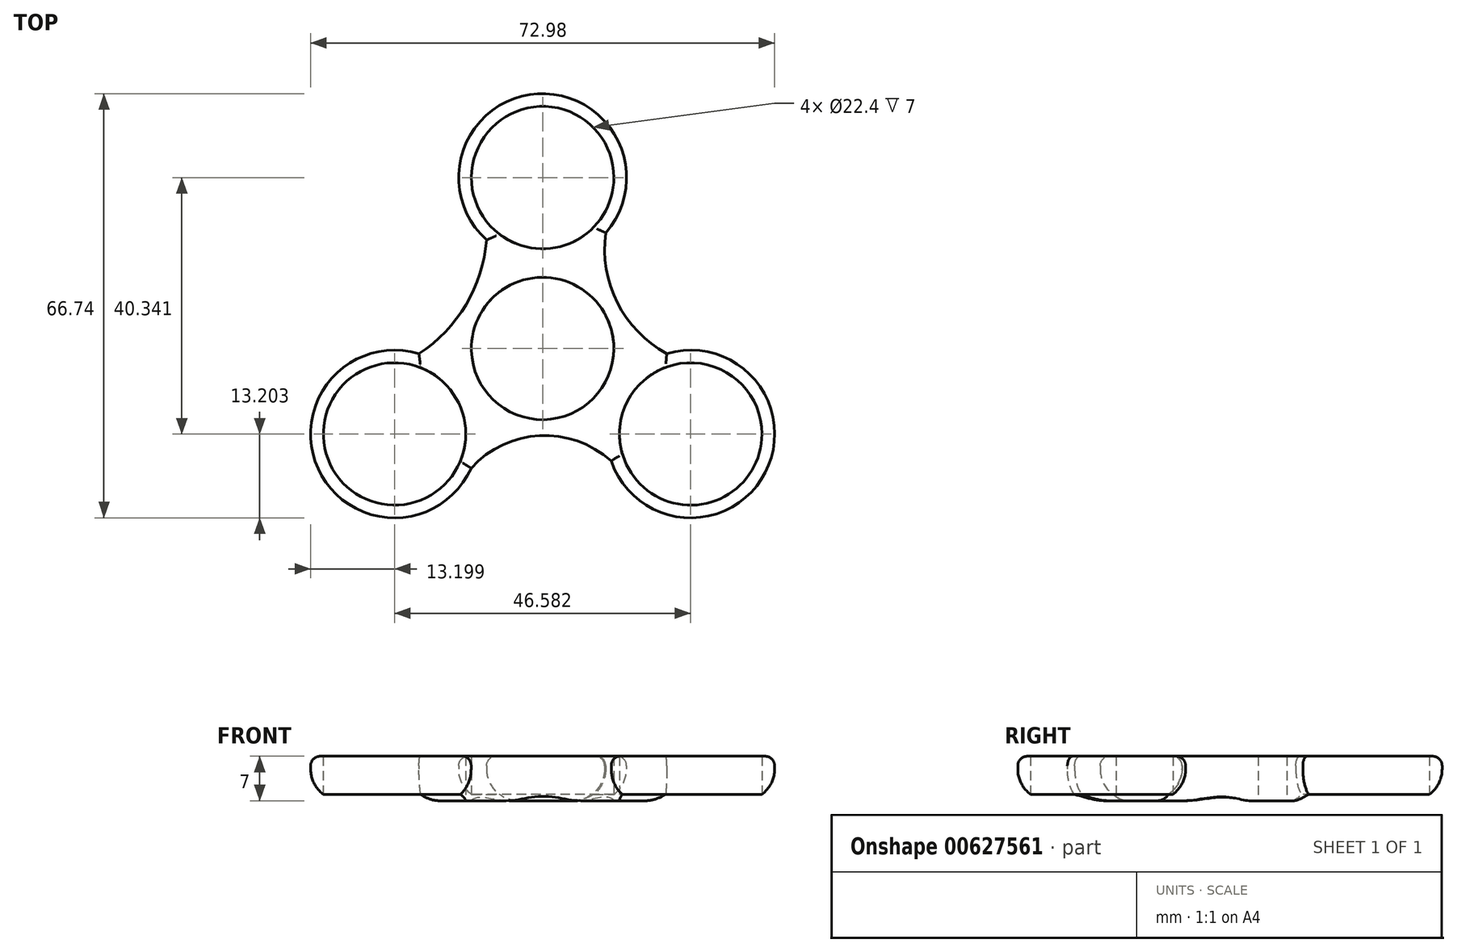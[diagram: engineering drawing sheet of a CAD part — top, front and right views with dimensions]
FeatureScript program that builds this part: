
annotation { "Feature Type Name" : "Feature", "Feature Type Description" : "" }
export const myFeature = defineFeature(function(context is Context, id is Id, definition is map)
    precondition{}
    {
        {
            var Q0;
            Q0=qCreatedBy(makeId("Top.planeOp"),FACE);
            var sketch = newSketch(context, id + "F0", { "sketchPlane" : qUnion([Q0])});
            skCircle(sketch, "E0", {"center": v(0, 0) * mm, "radius": 11.2 * mm});
            skCircle(sketch, "E1", {"center": v(0, 26.9) * mm, "radius": 11.2 * mm});
            skArc(sketch, "E2", {"start": v(9.92, 18.19) * mm, "mid": v(-0.78, 40.07) * mm, "end": v(-8.83, 17.08) * mm});
            skArc(sketch, "E3.1.0", {"start": v(-19.45, -0.82) * mm, "mid": v(-35.3, -18.92) * mm, "end": v(-11.24, -18.84) * mm});
            skCircle(sketch, "E3.1.1", {"center": v(-23.3, -13.45) * mm, "radius": 11.2 * mm});
            skArc(sketch, "E3.2.0", {"start": v(10.8, -17.7) * mm, "mid": v(35.02, -19.5) * mm, "end": v(19.53, -0.8) * mm});
            skCircle(sketch, "E3.2.1", {"center": v(23.3, -13.45) * mm, "radius": 11.2 * mm});
            skArc(sketch, "E4", {"start": v(-19.45, -0.82) * mm, "mid": v(-12.05, 6.9) * mm, "end": v(-8.83, 17.08) * mm});
            skArc(sketch, "E5", {"start": v(9.92, 18.19) * mm, "mid": v(11.76, 7.2) * mm, "end": v(19.53, -0.8) * mm});
            skArc(sketch, "E6", {"start": v(10.8, -17.7) * mm, "mid": v(-0.46, -13.71) * mm, "end": v(-11.24, -18.84) * mm});
            skSolve(sketch);
        }
        {
            var Q0;
            Q0=makeQuery(id+"F0.imprint","IMPRINT",FACE,{"disambiguationData":[TD([[makeQuery(id+"F0.imprint","IMPRINT",EDGE,{"derivedFrom":sQuery(id+"F0.wireOp",EDGE,"E0")}),-1.0]])]});
            extrude(context, id + "F1", {"entities" : qUnion([Q0]), "depth" : 7 * mm, "offsetDistance" : 25 * mm});
        }
        {
            var Q0;
            Q0=makeQuery(id+"F1.opExtrude","CAP_EDGE",EDGE,{"disambiguationData":[OSD([sQuery(id+"F0.wireOp",EDGE,"E6")])],"isStart":false});
            var Q1;
            Q1=makeQuery(id+"F1.opExtrude","CAP_EDGE",EDGE,{"disambiguationData":[OSD([sQuery(id+"F0.wireOp",EDGE,"E3.1.0")])],"isStart":false});
            var Q2;
            Q2=makeQuery(id+"F1.opExtrude","CAP_EDGE",EDGE,{"disambiguationData":[OSD([sQuery(id+"F0.wireOp",EDGE,"E4")])],"isStart":false});
            var Q3;
            Q3=makeQuery(id+"F1.opExtrude","CAP_EDGE",EDGE,{"disambiguationData":[OSD([sQuery(id+"F0.wireOp",EDGE,"E2")])],"isStart":false});
            var Q4;
            Q4=makeQuery(id+"F1.opExtrude","CAP_EDGE",EDGE,{"disambiguationData":[OSD([sQuery(id+"F0.wireOp",EDGE,"E3.2.0")])],"isStart":false});
            var Q5;
            Q5=makeQuery(id+"F1.opExtrude","CAP_EDGE",EDGE,{"disambiguationData":[OSD([sQuery(id+"F0.wireOp",EDGE,"E5")])],"isStart":false});
            fillet(context, id + "F2", {"entities" : qUnion([Q0, Q1, Q2, Q3, Q4, Q5]), "radius" : 1.5 * mm, "tangentPropagation" : true, "allowEdgeOverflow" : false});
        }
        {
            var Q0;
            Q0=makeQuery(id+"F1.opExtrude","CAP_EDGE",EDGE,{"disambiguationData":[OSD([sQuery(id+"F0.wireOp",EDGE,"E6")])],"isStart":true});
            var Q1;
            Q1=makeQuery(id+"F1.opExtrude","CAP_EDGE",EDGE,{"disambiguationData":[OSD([sQuery(id+"F0.wireOp",EDGE,"E3.2.0")])],"isStart":true});
            var Q2;
            Q2=makeQuery(id+"F1.opExtrude","CAP_EDGE",EDGE,{"disambiguationData":[OSD([sQuery(id+"F0.wireOp",EDGE,"E5")])],"isStart":true});
            var Q3;
            Q3=makeQuery(id+"F1.opExtrude","CAP_EDGE",EDGE,{"disambiguationData":[OSD([sQuery(id+"F0.wireOp",EDGE,"E2")])],"isStart":true});
            var Q4;
            Q4=makeQuery(id+"F1.opExtrude","CAP_EDGE",EDGE,{"disambiguationData":[OSD([sQuery(id+"F0.wireOp",EDGE,"E3.1.0")])],"isStart":true});
            var Q5;
            Q5=makeQuery(id+"F1.opExtrude","CAP_EDGE",EDGE,{"disambiguationData":[OSD([sQuery(id+"F0.wireOp",EDGE,"E4")])],"isStart":true});
            fillet(context, id + "F3", {"entities" : qUnion([Q0, Q1, Q2, Q3, Q4, Q5]), "radius" : 5 * mm, "tangentPropagation" : true, "allowEdgeOverflow" : false});
        }
    });
